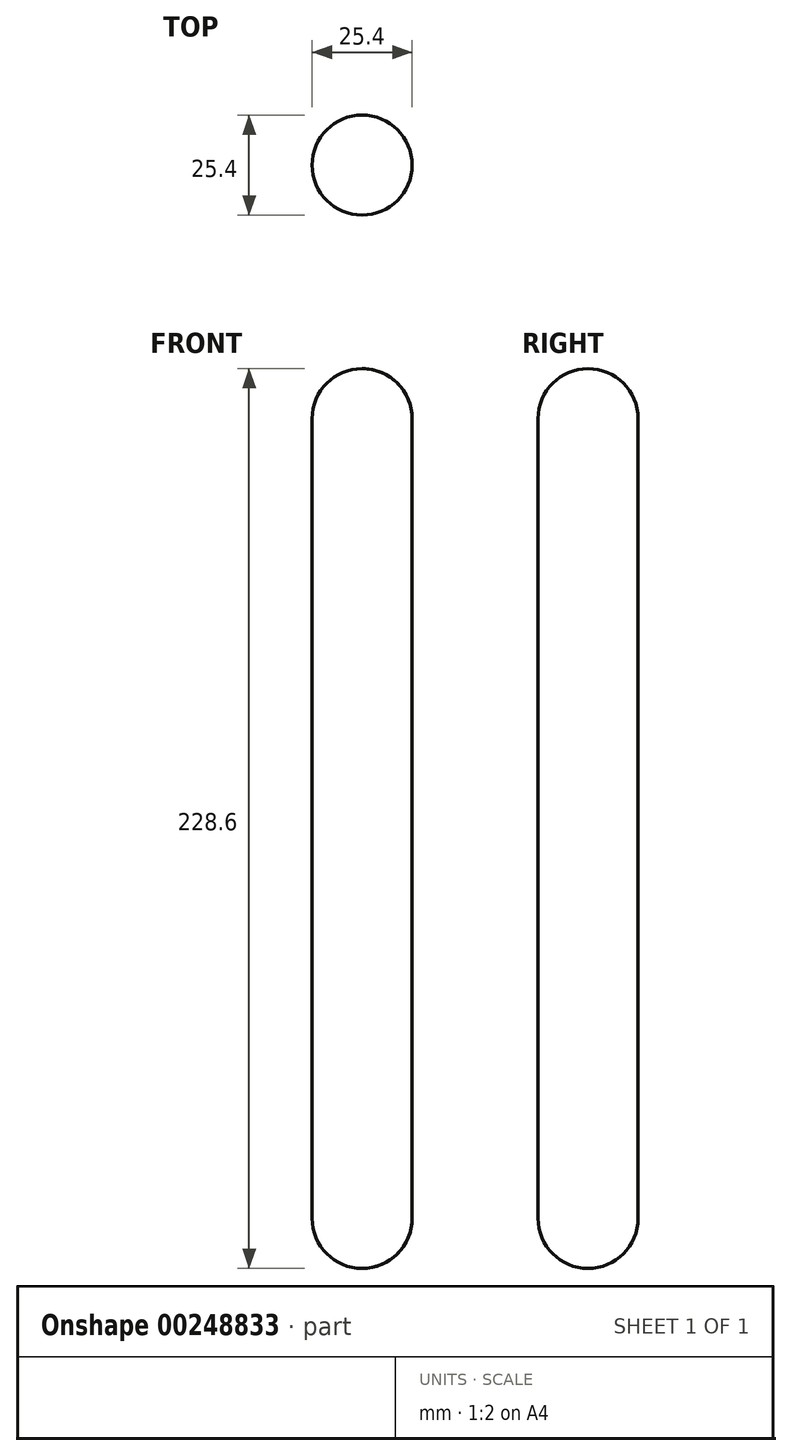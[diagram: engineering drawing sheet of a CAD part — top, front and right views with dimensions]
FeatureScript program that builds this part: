
annotation { "Feature Type Name" : "Feature", "Feature Type Description" : "" }
export const myFeature = defineFeature(function(context is Context, id is Id, definition is map)
    precondition{}
    {
        {
            var Q0;
            Q0=qCreatedBy(makeId("Top.planeOp"),FACE);
            var sketch = newSketch(context, id + "F0", { "sketchPlane" : qUnion([Q0])});
            skCircle(sketch, "E0", {"center": v(0, 0) * mm, "radius": 12.7 * mm});
            skSolve(sketch);
        }
        {
            var Q0;
            Q0=makeQuery(id+"F0.imprint","IMPRINT",FACE,{"disambiguationData":[TD([[makeQuery(id+"F0.imprint","IMPRINT",EDGE,{"derivedFrom":sQuery(id+"F0.wireOp",EDGE,"E0")}),1.0]])]});
            extrude(context, id + "F1", {"entities" : qUnion([Q0]), "depth" : 203.2 * mm});
        }
        {
            var Q0;
            Q0=qCreatedBy(makeId("Front.planeOp"),FACE);
            var sketch = newSketch(context, id + "F2", { "sketchPlane" : qUnion([Q0])});
            skLineSegment(sketch, "E1", {"start": v(0, 203.2) * mm, "end": v(0, 215.9) * mm});
            skLineSegment(sketch, "E2", {"start": v(0, 203.2) * mm, "end": v(12.7, 203.2) * mm});
            skArc(sketch, "E3", {"start": v(12.7, 203.2) * mm, "mid": v(8.98, 212.18) * mm, "end": v(0, 215.9) * mm});
            skLineSegment(sketch, "E4", {"start": v(0, 0) * mm, "end": v(0, -12.7) * mm});
            skLineSegment(sketch, "E5", {"start": v(0, 0) * mm, "end": v(12.7, 0) * mm});
            skArc(sketch, "E6", {"start": v(12.7, 0) * mm, "mid": v(8.98, -8.98) * mm, "end": v(0, -12.7) * mm});
            skSolve(sketch);
        }
        {
            var Q0;
            Q0=makeQuery(id+"F2.imprint","IMPRINT",FACE,{"disambiguationData":[TD([[makeQuery(id+"F2.imprint","IMPRINT",EDGE,{"derivedFrom":sQuery(id+"F2.wireOp",EDGE,"E1")}),-1.0]])]});
            var Q1;
            Q1=makeQuery(id+"F2.imprint","IMPRINT",FACE,{"disambiguationData":[TD([[makeQuery(id+"F2.imprint","IMPRINT",EDGE,{"derivedFrom":sQuery(id+"F2.wireOp",EDGE,"E4")}),1.0]])]});
            var Q2;
            Q2=sQuery(id+"F2.wireOp",EDGE,"E4");
            revolve(context, id + "F3", {"operationType" : NewBodyOperationType.ADD, "entities" : qUnion([Q0, Q1]), "axis" : qUnion([Q2]), "revolveType" : RevolveType.FULL});
        }
    });
